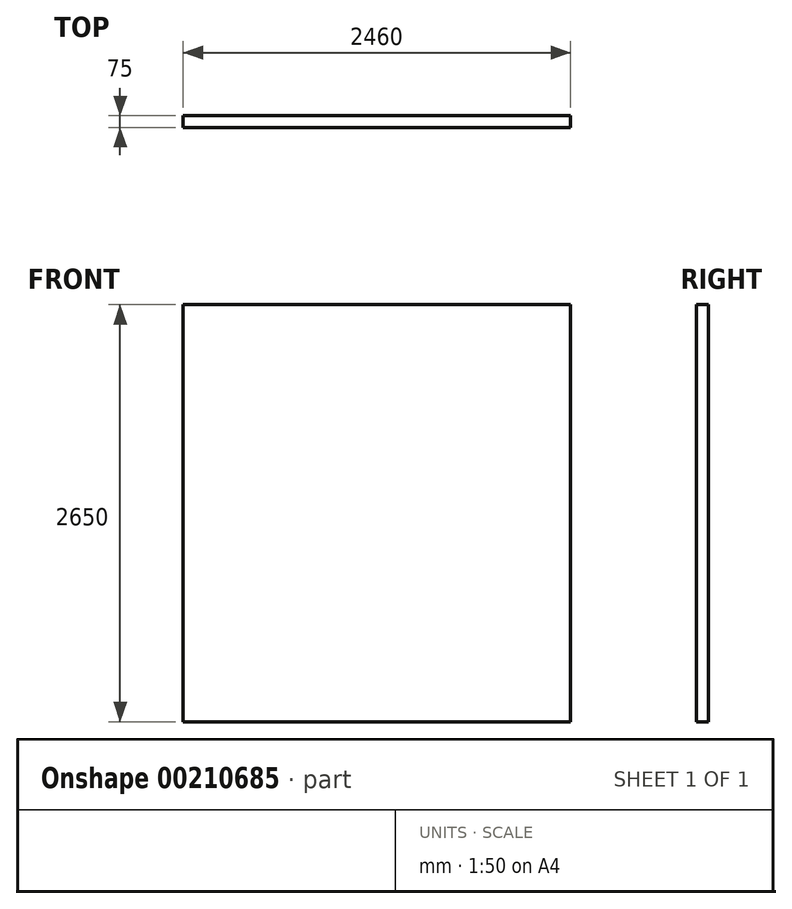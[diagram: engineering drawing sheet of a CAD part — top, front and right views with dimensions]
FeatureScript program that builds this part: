
annotation { "Feature Type Name" : "Feature", "Feature Type Description" : "" }
export const myFeature = defineFeature(function(context is Context, id is Id, definition is map)
    precondition{}
    {
        {
            var Q0;
            Q0=qCreatedBy(makeId("Front.planeOp"),FACE);
            var sketch = newSketch(context, id + "F0", { "sketchPlane" : qUnion([Q0])});
            skLineSegment(sketch, "E0.bottom", {"start": v(0, 0) * mm, "end": v(2460, 0) * mm});
            skLineSegment(sketch, "E0.left", {"start": v(0, 0) * mm, "end": v(0, 2650) * mm});
            skLineSegment(sketch, "E0.right", {"start": v(2460, 0) * mm, "end": v(2460, 2650) * mm});
            skLineSegment(sketch, "E1", {"start": v(0, 2650) * mm, "end": v(2460, 2650) * mm});
            skSolve(sketch);
        }
        {
            var Q0;
            Q0=makeQuery(id+"F0.imprint","IMPRINT",FACE,{"disambiguationData":[TD([[makeQuery(id+"F0.imprint","IMPRINT",EDGE,{"derivedFrom":sQuery(id+"F0.wireOp",EDGE,"E0.bottom")}),1.0]])]});
            extrude(context, id + "F1", {"entities" : qUnion([Q0]), "depth" : 75 * mm});
        }
    });
